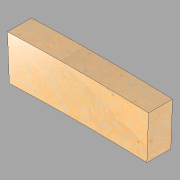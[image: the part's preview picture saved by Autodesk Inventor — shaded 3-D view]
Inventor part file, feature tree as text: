
AUTODESK INVENTOR PART (.ipt)
format: ipt  version: 2022.1 (Build 261234020, 234B)  size: 112,128 bytes
history: imported  units: in
note: dims shown in document units (in); Inventor stores cm internally (conversion verified against a paired STEP export)
features: imported_body x1
ambient origin geometry x8: Origin, YZ Plane, XZ Plane, XY Plane, X Axis, Y Axis, Z Axis, Center Point
bodies: Solid1 (imported_parasolid)
feature tree (1):
  imported_body  NMx_Import_Brep_tag  [imported B-rep: ~6 faces, bbox_mm=[898.52895, 280.549482, 152.4]]
